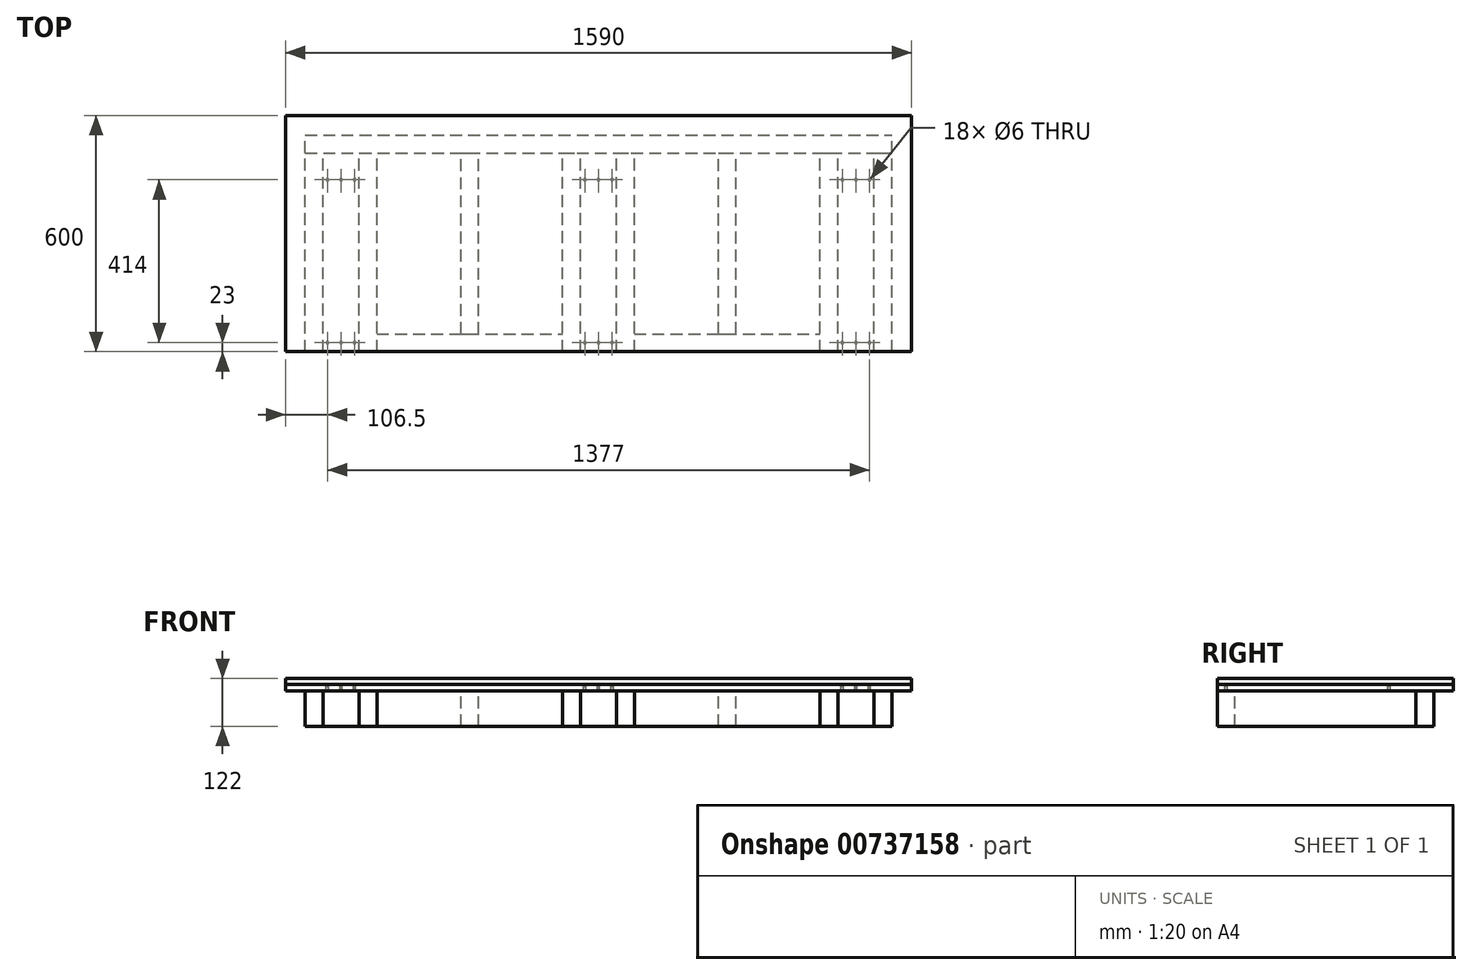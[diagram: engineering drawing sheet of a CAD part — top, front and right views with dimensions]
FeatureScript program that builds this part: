
annotation { "Feature Type Name" : "Feature", "Feature Type Description" : "" }
export const myFeature = defineFeature(function(context is Context, id is Id, definition is map)
    precondition{}
    {
        {
            var Q0;
            Q0=qCreatedBy(makeId("Top.planeOp"),FACE);
            var sketch = newSketch(context, id + "F0", { "sketchPlane" : qUnion([Q0])});
            skLineSegment(sketch, "E0.bottom", {"start": v(795, -300) * mm, "end": v(-795, -300) * mm});
            skLineSegment(sketch, "E0.top", {"start": v(795, 300) * mm, "end": v(-795, 300) * mm});
            skLineSegment(sketch, "E0.left", {"start": v(795, -300) * mm, "end": v(795, 300) * mm});
            skLineSegment(sketch, "E0.right", {"start": v(-795, -300) * mm, "end": v(-795, 300) * mm});
            skPoint(sketch, "E0.middle", {"position": v(0, 0) * mm});
            skSolve(sketch);
        }
        {
            var Q0;
            Q0 = qSketchRegion(id + "F0", true);
            extrude(context, id + "F1", {"entities" : qUnion([Q0]), "depth" : 16 * mm, "offsetDistance" : 25 * mm});
        }
        {
            var Q0;
            Q0=makeQuery(id+"F1.opExtrude","CAP_FACE",FACE,{"disambiguationData":[OSD([sQuery(id+"F0.wireOp",EDGE,"E0.bottom"),sQuery(id+"F0.wireOp",EDGE,"E0.top"),sQuery(id+"F0.wireOp",EDGE,"E0.left"),sQuery(id+"F0.wireOp",EDGE,"E0.right")])],"isStart":false});
            var sketch = newSketch(context, id + "F2", { "sketchPlane" : qUnion([Q0])});
            skLineSegment(sketch, "E1.0", {"start": v(795, -300) * mm, "end": v(-795, -300) * mm});
            skLineSegment(sketch, "E1.1", {"start": v(-795, -300) * mm, "end": v(-795, 300) * mm});
            skLineSegment(sketch, "E1.2", {"start": v(795, 300) * mm, "end": v(-795, 300) * mm});
            skLineSegment(sketch, "E1.3", {"start": v(795, -300) * mm, "end": v(795, 300) * mm});
            skSolve(sketch);
        }
        {
            var Q0;
            Q0 = qSketchRegion(id + "F2", true);
            extrude(context, id + "F3", {"entities" : qUnion([Q0]), "depth" : 16 * mm, "offsetDistance" : 25 * mm});
        }
        {
            var Q0;
            Q0=makeQuery(id+"F1.opExtrude","CAP_FACE",FACE,{"disambiguationData":[OSD([sQuery(id+"F0.wireOp",EDGE,"E0.bottom"),sQuery(id+"F0.wireOp",EDGE,"E0.top"),sQuery(id+"F0.wireOp",EDGE,"E0.left"),sQuery(id+"F0.wireOp",EDGE,"E0.right")])],"isStart":true});
            var sketch = newSketch(context, id + "F4", { "sketchPlane" : qUnion([Q0])});
            skLineSegment(sketch, "E2.bottom", {"start": v(-745, 300) * mm, "end": v(-700, 300) * mm});
            skLineSegment(sketch, "E2.top", {"start": v(-745, -205) * mm, "end": v(-700, -205) * mm});
            skLineSegment(sketch, "E2.left", {"start": v(-745, 300) * mm, "end": v(-745, -205) * mm});
            skLineSegment(sketch, "E2.right", {"start": v(-700, 300) * mm, "end": v(-700, -205) * mm});
            skLineSegment(sketch, "E3.bottom", {"start": v(-608, 300) * mm, "end": v(-563, 300) * mm});
            skLineSegment(sketch, "E3.top", {"start": v(-608, -205) * mm, "end": v(-563, -205) * mm});
            skLineSegment(sketch, "E3.left", {"start": v(-608, 300) * mm, "end": v(-608, -205) * mm});
            skLineSegment(sketch, "E3.right", {"start": v(-563, 300) * mm, "end": v(-563, -205) * mm});
            skLineSegment(sketch, "E4.bottom", {"start": v(-91, 300) * mm, "end": v(-46, 300) * mm});
            skLineSegment(sketch, "E4.top", {"start": v(-91, -205) * mm, "end": v(-46, -205) * mm});
            skLineSegment(sketch, "E4.left", {"start": v(-91, 300) * mm, "end": v(-91, -205) * mm});
            skLineSegment(sketch, "E4.right", {"start": v(-46, 300) * mm, "end": v(-46, -205) * mm});
            skLineSegment(sketch, "E5.bottom", {"start": v(46, 300) * mm, "end": v(91, 300) * mm});
            skLineSegment(sketch, "E5.top", {"start": v(46, -205) * mm, "end": v(91, -205) * mm});
            skLineSegment(sketch, "E5.left", {"start": v(46, 300) * mm, "end": v(46, -205) * mm});
            skLineSegment(sketch, "E5.right", {"start": v(91, 300) * mm, "end": v(91, -205) * mm});
            skLineSegment(sketch, "E6.bottom", {"start": v(563, 300) * mm, "end": v(608, 300) * mm});
            skLineSegment(sketch, "E6.top", {"start": v(563, -205) * mm, "end": v(608, -205) * mm});
            skLineSegment(sketch, "E6.left", {"start": v(563, 300) * mm, "end": v(563, -205) * mm});
            skLineSegment(sketch, "E6.right", {"start": v(608, 300) * mm, "end": v(608, -205) * mm});
            skLineSegment(sketch, "E7.bottom", {"start": v(700, 300) * mm, "end": v(745, 300) * mm});
            skLineSegment(sketch, "E7.top", {"start": v(700, -205) * mm, "end": v(745, -205) * mm});
            skLineSegment(sketch, "E7.left", {"start": v(700, 300) * mm, "end": v(700, -205) * mm});
            skLineSegment(sketch, "E7.right", {"start": v(745, 300) * mm, "end": v(745, -205) * mm});
            skLineSegment(sketch, "E8", {"start": v(-700, 47.5) * mm, "end": v(-608, 47.5) * mm, "construction": true});
            skLineSegment(sketch, "E9", {"start": v(-46, 47.5) * mm, "end": v(46, 47.5) * mm, "construction": true});
            skLineSegment(sketch, "E10", {"start": v(608, 47.5) * mm, "end": v(700, 47.5) * mm, "construction": true});
            skLineSegment(sketch, "E11", {"start": v(-563, 47.5) * mm, "end": v(-91, 47.5) * mm, "construction": true});
            skLineSegment(sketch, "E12", {"start": v(91, 47.5) * mm, "end": v(563, 47.5) * mm, "construction": true});
            skLineSegment(sketch, "E13", {"start": v(0, 47.5) * mm, "end": v(0, 300) * mm, "construction": true});
            skSolve(sketch);
        }
        {
            var Q0;
            Q0 = qSketchRegion(id + "F4", true);
            extrude(context, id + "F5", {"entities" : qUnion([Q0]), "depth" : 90 * mm, "offsetDistance" : 25 * mm});
        }
        {
            var Q0;
            Q0=makeQuery(id+"F1.opExtrude","CAP_FACE",FACE,{"disambiguationData":[OSD([sQuery(id+"F0.wireOp",EDGE,"E0.bottom"),sQuery(id+"F0.wireOp",EDGE,"E0.top"),sQuery(id+"F0.wireOp",EDGE,"E0.left"),sQuery(id+"F0.wireOp",EDGE,"E0.right")])],"isStart":true});
            var sketch = newSketch(context, id + "F6", { "sketchPlane" : qUnion([Q0])});
            skLineSegment(sketch, "E14.bottom", {"start": v(-745, -205) * mm, "end": v(745, -205) * mm});
            skLineSegment(sketch, "E14.top", {"start": v(-745, -250) * mm, "end": v(745, -250) * mm});
            skLineSegment(sketch, "E14.left", {"start": v(-745, -205) * mm, "end": v(-745, -250) * mm});
            skLineSegment(sketch, "E14.right", {"start": v(745, -205) * mm, "end": v(745, -250) * mm});
            skLineSegment(sketch, "E15.bottom", {"start": v(-563, 300) * mm, "end": v(-91, 300) * mm});
            skLineSegment(sketch, "E15.top", {"start": v(-563, 255) * mm, "end": v(-91, 255) * mm});
            skLineSegment(sketch, "E15.left", {"start": v(-563, 300) * mm, "end": v(-563, 255) * mm});
            skLineSegment(sketch, "E15.right", {"start": v(-91, 300) * mm, "end": v(-91, 255) * mm});
            skLineSegment(sketch, "E16.bottom", {"start": v(91, 300) * mm, "end": v(563, 300) * mm});
            skLineSegment(sketch, "E16.top", {"start": v(91, 255) * mm, "end": v(563, 255) * mm});
            skLineSegment(sketch, "E16.left", {"start": v(91, 300) * mm, "end": v(91, 255) * mm});
            skLineSegment(sketch, "E16.right", {"start": v(563, 300) * mm, "end": v(563, 255) * mm});
            skSolve(sketch);
        }
        {
            var Q0;
            Q0 = qSketchRegion(id + "F6", true);
            var Q1;
            Q1=makeQuery(id+"F5.opExtrude","CAP_FACE",FACE,{"disambiguationData":[OSD([sQuery(id+"F4.wireOp",EDGE,"E2.bottom"),sQuery(id+"F4.wireOp",EDGE,"E2.top"),sQuery(id+"F4.wireOp",EDGE,"E2.left"),sQuery(id+"F4.wireOp",EDGE,"E2.right")])],"isStart":false});
            extrude(context, id + "F7", {"entities" : qUnion([Q0]), "endBound" : BoundingType.UP_TO_SURFACE, "depth" : 25 * mm, "endBoundEntityFace" : qUnion([Q1]), "offsetDistance" : 25 * mm});
        }
        {
            var Q0;
            Q0=makeQuery(id+"F1.opExtrude","CAP_FACE",FACE,{"disambiguationData":[OSD([sQuery(id+"F0.wireOp",EDGE,"E0.bottom"),sQuery(id+"F0.wireOp",EDGE,"E0.top"),sQuery(id+"F0.wireOp",EDGE,"E0.left"),sQuery(id+"F0.wireOp",EDGE,"E0.right")])],"isStart":true});
            var sketch = newSketch(context, id + "F8", { "sketchPlane" : qUnion([Q0])});
            skLineSegment(sketch, "E17.bottom", {"start": v(-349.5, 255) * mm, "end": v(-304.5, 255) * mm});
            skLineSegment(sketch, "E17.top", {"start": v(-349.5, -205) * mm, "end": v(-304.5, -205) * mm});
            skLineSegment(sketch, "E17.left", {"start": v(-349.5, 255) * mm, "end": v(-349.5, -205) * mm});
            skLineSegment(sketch, "E17.right", {"start": v(-304.5, 255) * mm, "end": v(-304.5, -205) * mm});
            skLineSegment(sketch, "E18.bottom", {"start": v(304.5, 255) * mm, "end": v(349.5, 255) * mm});
            skLineSegment(sketch, "E18.top", {"start": v(304.5, -205) * mm, "end": v(349.5, -205) * mm});
            skLineSegment(sketch, "E18.left", {"start": v(304.5, 255) * mm, "end": v(304.5, -205) * mm});
            skLineSegment(sketch, "E18.right", {"start": v(349.5, 255) * mm, "end": v(349.5, -205) * mm});
            skSolve(sketch);
        }
        {
            var Q0;
            Q0 = qSketchRegion(id + "F8", true);
            var Q1;
            Q1=makeQuery(id+"F5.opExtrude","CAP_FACE",FACE,{"disambiguationData":[OSD([sQuery(id+"F4.wireOp",EDGE,"E2.bottom"),sQuery(id+"F4.wireOp",EDGE,"E2.top"),sQuery(id+"F4.wireOp",EDGE,"E2.left"),sQuery(id+"F4.wireOp",EDGE,"E2.right")])],"isStart":false});
            extrude(context, id + "F9", {"entities" : qUnion([Q0]), "endBound" : BoundingType.UP_TO_SURFACE, "depth" : 25 * mm, "endBoundEntityFace" : qUnion([Q1]), "offsetDistance" : 25 * mm});
        }
        {
            var Q0;
            Q0=makeQuery(id+"F1.opExtrude","CAP_FACE",FACE,{"disambiguationData":[OSD([sQuery(id+"F0.wireOp",EDGE,"E0.bottom"),sQuery(id+"F0.wireOp",EDGE,"E0.top"),sQuery(id+"F0.wireOp",EDGE,"E0.left"),sQuery(id+"F0.wireOp",EDGE,"E0.right")])],"isStart":true});
            var sketch = newSketch(context, id + "F10", { "sketchPlane" : qUnion([Q0])});
            skPoint(sketch, "E19", {"position": v(-688.5, -137) * mm});
            skPoint(sketch, "E20", {"position": v(-654, -137) * mm});
            skPoint(sketch, "E21", {"position": v(-619.5, -137) * mm});
            skPoint(sketch, "E22", {"position": v(-34.5, -137) * mm});
            skPoint(sketch, "E23", {"position": v(0, -137) * mm});
            skPoint(sketch, "E24", {"position": v(34.5, -137) * mm});
            skPoint(sketch, "E25", {"position": v(619.5, -137) * mm});
            skPoint(sketch, "E26", {"position": v(654, -137) * mm});
            skPoint(sketch, "E27", {"position": v(688.5, -137) * mm});
            skPoint(sketch, "E28", {"position": v(688.5, 277) * mm});
            skPoint(sketch, "E29", {"position": v(654, 277) * mm});
            skPoint(sketch, "E30", {"position": v(619.5, 277) * mm});
            skPoint(sketch, "E31", {"position": v(34.5, 277) * mm});
            skPoint(sketch, "E32", {"position": v(0, 277) * mm});
            skPoint(sketch, "E33", {"position": v(-34.5, 277) * mm});
            skPoint(sketch, "E34", {"position": v(-619.5, 277) * mm});
            skPoint(sketch, "E35", {"position": v(-654, 277) * mm});
            skPoint(sketch, "E36", {"position": v(-688.5, 277) * mm});
            skLineSegment(sketch, "E37", {"start": v(-688.5, -137) * mm, "end": v(-654, -137) * mm, "construction": true});
            skLineSegment(sketch, "E38", {"start": v(-619.5, -137) * mm, "end": v(-654, -137) * mm, "construction": true});
            skLineSegment(sketch, "E39", {"start": v(-34.5, -137) * mm, "end": v(0, -137) * mm, "construction": true});
            skLineSegment(sketch, "E40", {"start": v(0, -137) * mm, "end": v(34.5, -137) * mm, "construction": true});
            skLineSegment(sketch, "E41", {"start": v(619.5, -137) * mm, "end": v(654, -137) * mm, "construction": true});
            skLineSegment(sketch, "E42", {"start": v(654, -137) * mm, "end": v(688.5, -137) * mm, "construction": true});
            skLineSegment(sketch, "E43", {"start": v(619.5, 277) * mm, "end": v(654, 277) * mm, "construction": true});
            skLineSegment(sketch, "E44", {"start": v(654, 277) * mm, "end": v(688.5, 277) * mm, "construction": true});
            skLineSegment(sketch, "E45", {"start": v(-34.5, 277) * mm, "end": v(0, 277) * mm, "construction": true});
            skLineSegment(sketch, "E46", {"start": v(0, 277) * mm, "end": v(34.5, 277) * mm, "construction": true});
            skLineSegment(sketch, "E47", {"start": v(-688.5, 277) * mm, "end": v(-654, 277) * mm, "construction": true});
            skLineSegment(sketch, "E48", {"start": v(-619.5, 277) * mm, "end": v(-654, 277) * mm, "construction": true});
            skLineSegment(sketch, "E49", {"start": v(-688.5, -137) * mm, "end": v(-700, -137) * mm, "construction": true});
            skLineSegment(sketch, "E50", {"start": v(-619.5, -137) * mm, "end": v(-608, -137) * mm, "construction": true});
            skLineSegment(sketch, "E51", {"start": v(688.5, -137) * mm, "end": v(700, -137) * mm, "construction": true});
            skLineSegment(sketch, "E52", {"start": v(619.5, -137) * mm, "end": v(608, -137) * mm, "construction": true});
            skSolve(sketch);
        }
        {
            var Q0;
            Q0=sQuery(id+"F10.wireOp",VERTEX,"E36");
            var Q1;
            Q1=sQuery(id+"F10.wireOp",VERTEX,"E35");
            var Q2;
            Q2=sQuery(id+"F10.wireOp",VERTEX,"E34");
            var Q3;
            Q3=sQuery(id+"F10.wireOp",VERTEX,"E19");
            var Q4;
            Q4=sQuery(id+"F10.wireOp",VERTEX,"E20");
            var Q5;
            Q5=sQuery(id+"F10.wireOp",VERTEX,"E21");
            var Q6;
            Q6=sQuery(id+"F10.wireOp",VERTEX,"E22");
            var Q7;
            Q7=sQuery(id+"F10.wireOp",VERTEX,"E23");
            var Q8;
            Q8=sQuery(id+"F10.wireOp",VERTEX,"E24");
            var Q9;
            Q9=sQuery(id+"F10.wireOp",VERTEX,"E33");
            var Q10;
            Q10=sQuery(id+"F10.wireOp",VERTEX,"E32");
            var Q11;
            Q11=sQuery(id+"F10.wireOp",VERTEX,"E31");
            var Q12;
            Q12=sQuery(id+"F10.wireOp",VERTEX,"E30");
            var Q13;
            Q13=sQuery(id+"F10.wireOp",VERTEX,"E29");
            var Q14;
            Q14=sQuery(id+"F10.wireOp",VERTEX,"E28");
            var Q15;
            Q15=sQuery(id+"F10.wireOp",VERTEX,"E25");
            var Q16;
            Q16=sQuery(id+"F10.wireOp",VERTEX,"E26");
            var Q17;
            Q17=sQuery(id+"F10.wireOp",VERTEX,"E27");
            var Q18;
            Q18=makeQuery(id+"F1.opExtrude","SWEPT_BODY",BODY,{"disambiguationData":[OSD([sQuery(id+"F0.wireOp",EDGE,"E0.bottom"),sQuery(id+"F0.wireOp",EDGE,"E0.top"),sQuery(id+"F0.wireOp",EDGE,"E0.left"),sQuery(id+"F0.wireOp",EDGE,"E0.right")])]});
            hole(context, id + "F11", {"style" : HoleStyle.SIMPLE, "endStyle" : HoleEndStyle.BLIND, "holeDiameter" : 6 * mm, "majorDiameter" : 5 * mm, "holeDepth" : 12 * mm, "isTappedThrough" : true, "tappedDepth" : 12 * mm, "tapClearance" : 3, "locations" : qUnion([Q0, Q1, Q2, Q3, Q4, Q5, Q6, Q7, Q8, Q9, Q10, Q11, Q12, Q13, Q14, Q15, Q16, Q17]), "scope" : qUnion([Q18]), "startStyle" : HoleStartStyle.PART});
        }
    });
